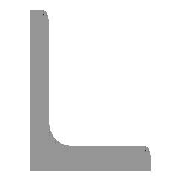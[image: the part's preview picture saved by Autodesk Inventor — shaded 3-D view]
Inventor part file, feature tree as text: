
AUTODESK INVENTOR PART (.ipt)
format: ipt  version: 2016 (Build 200138000, 138)  size: 120,320 bytes
history: native  units: mm (DEFAULTED — no unit token found)
features: other x4, sketch x2, extrude x1, plane x1
ambient origin geometry x8: Origin, YZ Plane, XZ Plane, XY Plane, X Axis, Y Axis, Z Axis, Center Point
bodies: Solid1 (feature_tree)
feature tree (8):
  parser-record x1  (decoder bookkeeping rows leaked as tree rows — omitted from the tree; the rows remain in map.json)
  other  "Driven Length"
  other  "Plano inicial"
  other  "Plano final"
  extrude  "Cuerpo"  Depth=38.1mm
  sketch  "Sketch3"  dims[d0=38.1mm d1=38.1mm]
  plane  "Work Plane3"
  sketch  "Sketch4"  dims[d2=4.7625mm d3=4.7625mm d4=1401.0mm d5=0.0mm d10=0.0mm d11=0.0mm d12=-0.0mm d13=1401.0mm d14=4.826mm d15=2.286mm d16=90.0deg d17=1401.0mm]
